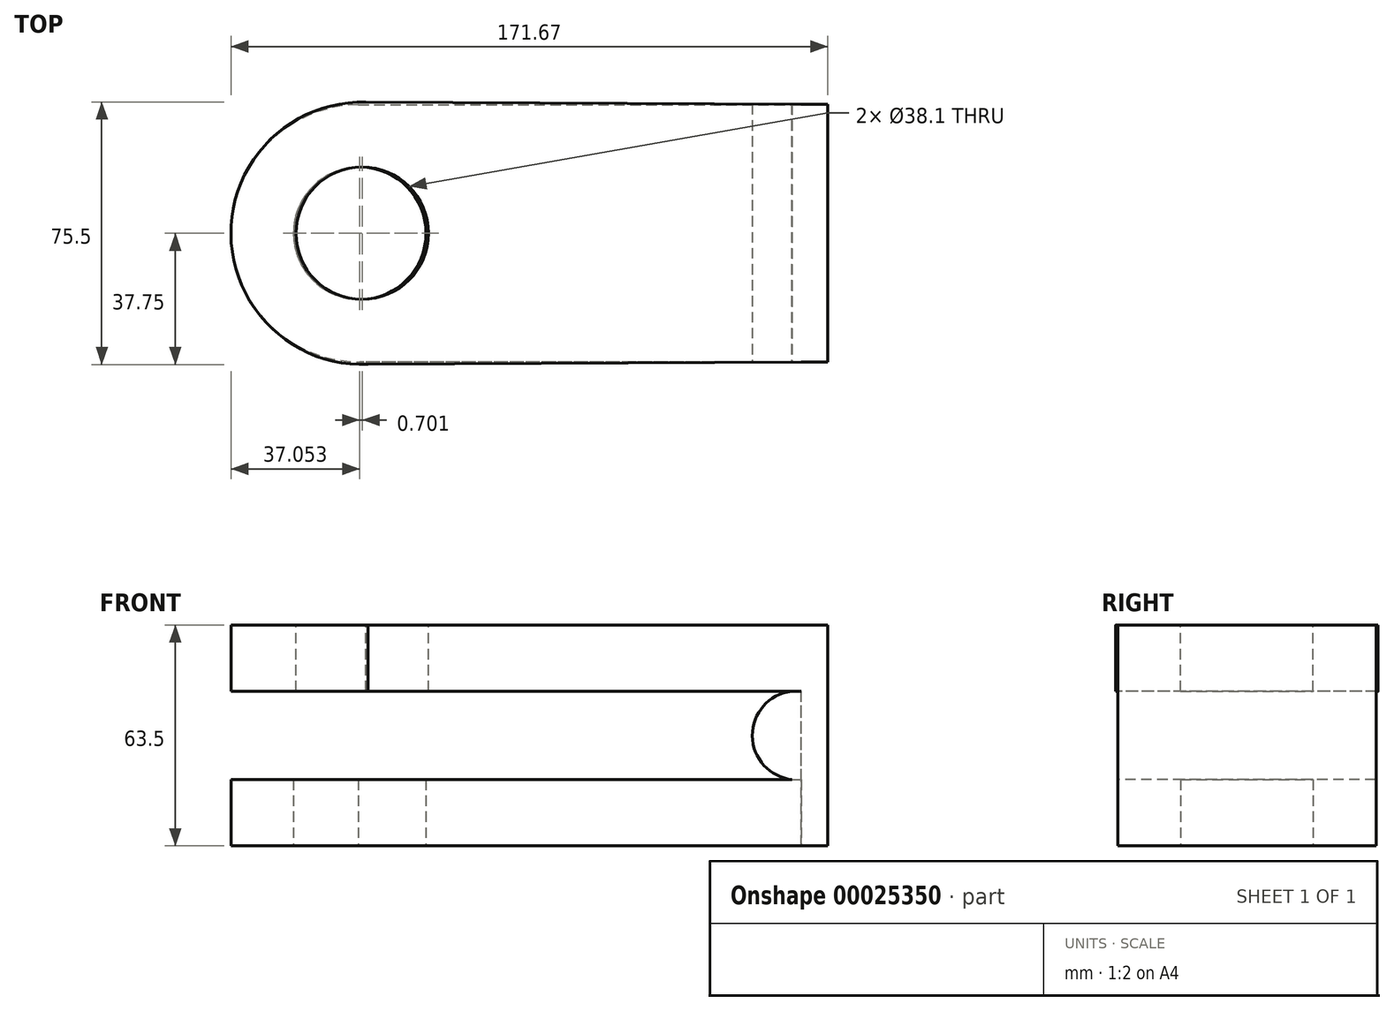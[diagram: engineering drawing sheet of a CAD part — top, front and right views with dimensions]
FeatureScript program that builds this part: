
annotation { "Feature Type Name" : "Feature", "Feature Type Description" : "" }
export const myFeature = defineFeature(function(context is Context, id is Id, definition is map)
    precondition{}
    {
        {
            var Q0;
            Q0=qCreatedBy(makeId("Top.planeOp"),FACE);
            var sketch = newSketch(context, id + "F0", { "sketchPlane" : qUnion([Q0])});
            skCircle(sketch, "E0", {"center": v(-75.92, 0) * mm, "radius": 37.04 * mm});
            skCircle(sketch, "E1", {"center": v(-75.92, 0) * mm, "radius": 19.05 * mm});
            skLineSegment(sketch, "E2", {"start": v(-76.3, 37.04) * mm, "end": v(51.08, 37.04) * mm});
            skLineSegment(sketch, "E3", {"start": v(51.08, 37.04) * mm, "end": v(51.08, -37.04) * mm});
            skLineSegment(sketch, "E4", {"start": v(51.08, -37.04) * mm, "end": v(-75.92, -37.04) * mm});
            skSolve(sketch);
        }
        {
            var Q0;
            Q0=makeQuery(id+"F0.imprint","IMPRINT",FACE,{"disambiguationData":[TD([[makeQuery(id+"F0.imprint","IMPRINT",EDGE,{"derivedFrom":sQuery(id+"F0.wireOp",EDGE,"E1")}),-1.0]])]});
            var Q1;
            {var subQ1=sQuery(id+"F0.wireOp",EDGE,"E3");Q1=makeQuery(id+"F0.imprint","IMPRINT",FACE,{"disambiguationData":[TD([[makeQuery(id+"F0.imprint","IMPRINT",EDGE,{"derivedFrom":subQ1}),-1.0]])]});}
            extrude(context, id + "F1", {"entities" : qUnion([Q0, Q1]), "depth" : 19.05 * mm});
        }
        {
            var Q0;
            Q0=makeQuery(id+"F1.opExtrude","SWEPT_FACE",FACE,{"disambiguationData":[OSD([sQuery(id+"F0.wireOp",EDGE,"E3")])]});
            var sketch = newSketch(context, id + "F2", { "sketchPlane" : qUnion([Q0])});
            skLineSegment(sketch, "E5.bottom", {"start": v(-37.04, 0) * mm, "end": v(37.16, 0) * mm});
            skLineSegment(sketch, "E5.top", {"start": v(-37.04, 63.5) * mm, "end": v(37.16, 63.5) * mm});
            skLineSegment(sketch, "E5.left", {"start": v(-37.04, 0) * mm, "end": v(-37.04, 63.5) * mm});
            skLineSegment(sketch, "E5.right", {"start": v(37.16, 0) * mm, "end": v(37.16, 63.5) * mm});
            skSolve(sketch);
        }
        {
            var Q0;
            {var subQ4=sQuery(id+"F2.wireOp",EDGE,"E5.top");Q0=makeQuery(id+"F2.imprint","IMPRINT",FACE,{"disambiguationData":[TD([[makeQuery(id+"F2.imprint","IMPRINT",EDGE,{"derivedFrom":subQ4}),-1.0]])]});}
            var Q1;
            {var subQ0=sQuery(id+"F0.wireOp",EDGE,"E3");var subQ1=makeQuery(id+"F1.opExtrude","CAP_EDGE",EDGE,{"disambiguationData":[OSD([subQ0])],"isStart":false});Q1=makeQuery(id+"F2.imprint","IMPRINT",FACE,{"disambiguationData":[TD([[makeQuery(id+"F2.imprint","IMPRINT",EDGE,{"derivedFrom":subQ1}),1.0]])]});}
            extrude(context, id + "F3", {"entities" : qUnion([Q0, Q1]), "operationType" : NewBodyOperationType.ADD, "depth" : 7.62 * mm});
        }
        {
            var Q0;
            Q0=makeQuery(id+"F3.opExtrude","CAP_FACE",FACE,{"disambiguationData":[OSD([sQuery(id+"F2.wireOp",EDGE,"E5.bottom"),sQuery(id+"F2.wireOp",EDGE,"E5.top"),sQuery(id+"F2.wireOp",EDGE,"E5.left"),sQuery(id+"F2.wireOp",EDGE,"E5.right")])],"isStart":true});
            var sketch = newSketch(context, id + "F4", { "sketchPlane" : qUnion([Q0])});
            skLineSegment(sketch, "E6", {"start": v(-37.16, 63.5) * mm, "end": v(37.04, 63.5) * mm});
            skLineSegment(sketch, "E7", {"start": v(37.04, 63.5) * mm, "end": v(37.04, 44.45) * mm});
            skLineSegment(sketch, "E8", {"start": v(37.04, 44.45) * mm, "end": v(-37.16, 44.45) * mm});
            skLineSegment(sketch, "E9", {"start": v(-37.16, 44.45) * mm, "end": v(-37.16, 63.5) * mm});
            skSolve(sketch);
        }
        {
            var Q0;
            Q0=makeQuery(id+"FLVy33Wq20wkKmN_1.boolean.opBoolean","MERGE",FACE,{"derivedFrom":[makeQuery(id+"FOULcimmuMPFlLA_1.boolean.opBoolean","MERGE",FACE,{"derivedFrom":[makeQuery(id+"F3.opExtrude","SWEPT_FACE",FACE,{"disambiguationData":[OSD([sQuery(id+"F2.wireOp",EDGE,"E5.top")])]}),makeQuery(id+"FOULcimmuMPFlLA_1.opExtrude","SWEPT_FACE",FACE,{"disambiguationData":[OSD([sQuery(id+"F4.wireOp",EDGE,"E6")])]})]}),makeQuery(id+"FLVy33Wq20wkKmN_1.opExtrude","CAP_FACE",FACE,{"disambiguationData":[OSD([sQuery(id+"FCmgK9SPQJfkYBM_1.wireOp",EDGE,"c7f06e6d-d900-4d23-b185-7ea05f1f8e68"),sQuery(id+"FCmgK9SPQJfkYBM_1.wireOp",EDGE,"7e05d032-9bfb-4e7d-a4a8-e59e54e998bc")])],"isStart":true})]});
            var sketch = newSketch(context, id + "F5", { "sketchPlane" : qUnion([Q0])});
            skCircle(sketch, "E10", {"center": v(-75.22, 0) * mm, "radius": 37.75 * mm});
            skCircle(sketch, "E11", {"center": v(-75.22, 0) * mm, "radius": 19.05 * mm});
            skLineSegment(sketch, "E12", {"start": v(58.7, 37.16) * mm, "end": v(58.7, -37.04) * mm});
            skLineSegment(sketch, "E13", {"start": v(-76.49, -37.73) * mm, "end": v(51.08, -37.04) * mm});
            skLineSegment(sketch, "E14", {"start": v(-75.96, 37.74) * mm, "end": v(51.08, 37.16) * mm});
            skLineSegment(sketch, "E15", {"start": v(51.08, 37.16) * mm, "end": v(51.08, -37.04) * mm});
            skSolve(sketch);
        }
        {
            var Q0;
            Q0 = qSketchRegion(id + "F5", true);
            extrude(context, id + "F6", {"entities" : qUnion([Q0]), "oppositeDirection" : true, "depth" : 19.05 * mm});
        }
        {
            var Q0;
            Q0=makeQuery(id+"F3.boolean.opBoolean","MERGE",FACE,{"derivedFrom":[makeQuery(id+"F1.opExtrude","SWEPT_FACE",FACE,{"disambiguationData":[OSD([sQuery(id+"F0.wireOp",EDGE,"E4")])]}),makeQuery(id+"F3.opExtrude","SWEPT_FACE",FACE,{"disambiguationData":[OSD([sQuery(id+"F2.wireOp",EDGE,"E5.left")])]})]});
            var sketch = newSketch(context, id + "F7", { "sketchPlane" : qUnion([Q0])});
            skArc(sketch, "E16", {"start": v(51.08, 44.48) * mm, "mid": v(36.97, 31.76) * mm, "end": v(51.08, 19.05) * mm});
            skLineSegment(sketch, "E17", {"start": v(58.7, 0) * mm, "end": v(58.7, 63.5) * mm});
            skSolve(sketch);
        }
        {
            var Q0;
            Q0 = qSketchRegion(id + "F7", true);
            var Q1;
            {var subQ0=makeQuery(id+"F3.opExtrude","CAP_EDGE",EDGE,{"disambiguationData":[OSD([sQuery(id+"F2.wireOp",EDGE,"E5.left")])],"isStart":true});var subQ1=sQuery(id+"F7.wireOp",EDGE,"E16");var subQ2=makeQuery(id+"F7.imprint","INTERSECT",VERTEX,{"derivedFrom":[subQ0,subQ1]});Q1=makeQuery(id+"F7.imprint","IMPRINT",FACE,{"disambiguationData":[TD([[makeQuery(id+"F7.imprint","IMPRINT",EDGE,{"disambiguationData":[TD([[subQ2,-1.0]])],"derivedFrom":subQ1}),1.0]])]});}
            extrude(context, id + "F8", {"entities" : qUnion([Q0, Q1]), "operationType" : NewBodyOperationType.ADD, "oppositeDirection" : true, "depth" : 74.2 * mm});
        }
    });
